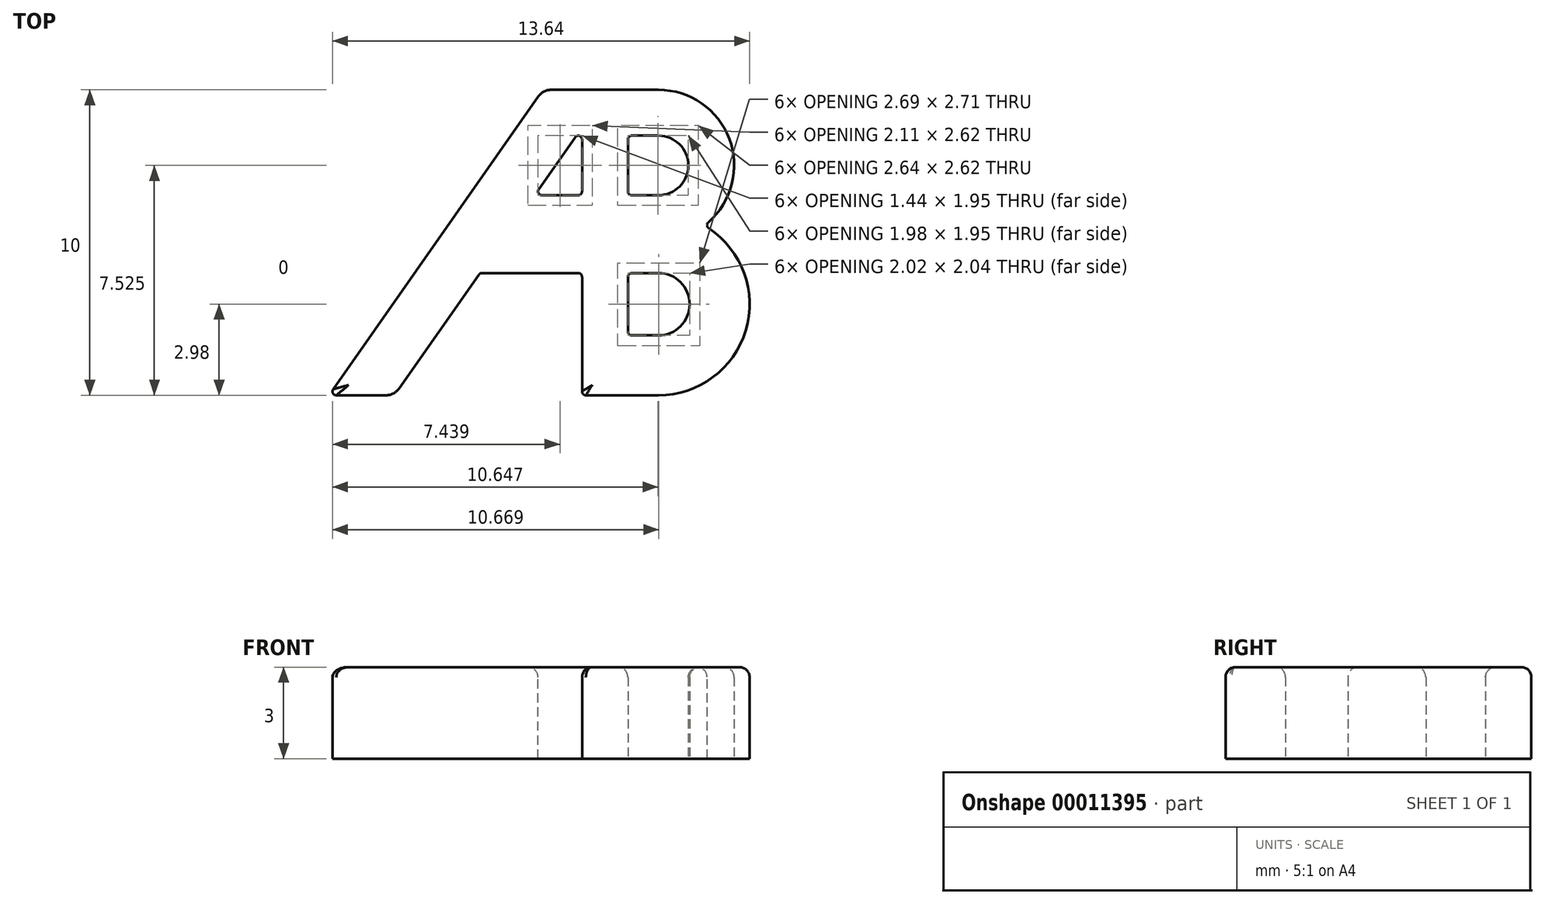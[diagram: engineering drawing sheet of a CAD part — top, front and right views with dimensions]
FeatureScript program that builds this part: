
annotation { "Feature Type Name" : "Feature", "Feature Type Description" : "" }
export const myFeature = defineFeature(function(context is Context, id is Id, definition is map)
    precondition{}
    {
        {
            assignVariable(context, id + "F0", {"name" : "Height", "anyValue" : 10});
        }
        {
            var Q0;
            Q0=qCreatedBy(makeId("Top.planeOp"),FACE);
            var sketch = newSketch(context, id + "F1", { "sketchPlane" : qUnion([Q0])});
            skLineSegment(sketch, "E0", {"start": v(-6.88, -5) * mm, "end": v(0.12, 5) * mm});
            skLineSegment(sketch, "E1", {"start": v(0.12, 5) * mm, "end": v(3.9, 5) * mm});
            skArc(sketch, "E2", {"start": v(3.9, 5) * mm, "mid": v(6.24, 3.32) * mm, "end": v(5.4, 0.56) * mm});
            skLineSegment(sketch, "E3", {"start": v(1.4, -5) * mm, "end": v(3.9, -5) * mm});
            skArc(sketch, "E4", {"start": v(3.9, -5) * mm, "mid": v(6.78, -2.8) * mm, "end": v(5.4, 0.56) * mm});
            skLineSegment(sketch, "E5", {"start": v(1.4, -5) * mm, "end": v(1.4, -1) * mm});
            skLineSegment(sketch, "E6", {"start": v(1.4, -1) * mm, "end": v(-1.94, -1) * mm});
            skLineSegment(sketch, "E7", {"start": v(-1.94, -1) * mm, "end": v(-4.74, -5) * mm});
            skLineSegment(sketch, "E8", {"start": v(-4.74, -5) * mm, "end": v(-6.88, -5) * mm});
            skLineSegment(sketch, "E9", {"start": v(3.9, -5) * mm, "end": v(3.9, 5) * mm, "construction": true});
            skLineSegment(sketch, "E10", {"start": v(3.9, 1.55) * mm, "end": v(2.9, 1.55) * mm});
            skArc(sketch, "E11", {"start": v(3.9, 3.5) * mm, "mid": v(4.87, 2.52) * mm, "end": v(3.9, 1.55) * mm});
            skLineSegment(sketch, "E12", {"start": v(3.9, 3.5) * mm, "end": v(2.9, 3.5) * mm});
            skLineSegment(sketch, "E13", {"start": v(2.9, -3.04) * mm, "end": v(2.9, -1) * mm});
            skLineSegment(sketch, "E14", {"start": v(2.9, -1) * mm, "end": v(3.9, -1) * mm});
            skArc(sketch, "E15", {"start": v(3.9, -1) * mm, "mid": v(4.92, -2.02) * mm, "end": v(3.9, -3.04) * mm});
            skLineSegment(sketch, "E16", {"start": v(2.9, -3.04) * mm, "end": v(3.9, -3.04) * mm});
            skLineSegment(sketch, "E17", {"start": v(2.9, 1.55) * mm, "end": v(2.9, 3.5) * mm});
            skLineSegment(sketch, "E18", {"start": v(1.4, 3.38) * mm, "end": v(1.4, 1.55) * mm});
            skLineSegment(sketch, "E19", {"start": v(1.4, 1.55) * mm, "end": v(-0.16, 1.55) * mm});
            skLineSegment(sketch, "E20", {"start": v(-0.16, 1.55) * mm, "end": v(1.17, 3.45) * mm});
            skLineSegment(sketch, "E21.bottom", {"start": v(-6.88, -5) * mm, "end": v(6.88, -5) * mm, "construction": true});
            skLineSegment(sketch, "E21.top", {"start": v(-6.88, 5) * mm, "end": v(6.88, 5) * mm, "construction": true});
            skLineSegment(sketch, "E21.left", {"start": v(-6.88, -5) * mm, "end": v(-6.88, 5) * mm, "construction": true});
            skLineSegment(sketch, "E21.right", {"start": v(6.88, -5) * mm, "end": v(6.88, 5) * mm, "construction": true});
            skLineSegment(sketch, "E22", {"start": v(-6.88, 5) * mm, "end": v(6.88, -5) * mm, "construction": true});
            skPoint(sketch, "E23.visualSharp", {"position": v(1.4, 3.77) * mm});
            skArc(sketch, "E23.filletArc", {"start": v(1.4, 3.38) * mm, "mid": v(1.31, 3.5) * mm, "end": v(1.17, 3.45) * mm});
            skLineSegment(sketch, "E24", {"start": v(2.9, 3.5) * mm, "end": v(-2.48, 3.5) * mm, "construction": true});
            skSolve(sketch);
        }
        {
            var Q0;
            Q0 = qSketchRegion(id + "F1", true);
            extrude(context, id + "F2", {"entities" : qUnion([Q0]), "depth" : 3 * mm, "offsetDistance" : 25 * mm});
        }
        {
            var Q0;
            Q0=makeQuery(id+"F2.opExtrude","SWEPT_EDGE",EDGE,{"disambiguationData":[OSD([sQuery(id+"F1.wireOp",EDGE,"E18"),sQuery(id+"F1.wireOp",EDGE,"E19")])]});
            var Q1;
            Q1=makeQuery(id+"F2.opExtrude","SWEPT_EDGE",EDGE,{"disambiguationData":[OSD([sQuery(id+"F1.wireOp",EDGE,"E19"),sQuery(id+"F1.wireOp",EDGE,"E20")])]});
            var Q2;
            Q2=makeQuery(id+"F2.opExtrude","SWEPT_EDGE",EDGE,{"disambiguationData":[OSD([sQuery(id+"F1.wireOp",EDGE,"E0"),sQuery(id+"F1.wireOp",EDGE,"E8")])]});
            var Q3;
            Q3=makeQuery(id+"F2.opExtrude","SWEPT_EDGE",EDGE,{"disambiguationData":[OSD([sQuery(id+"F1.wireOp",EDGE,"E6"),sQuery(id+"F1.wireOp",EDGE,"E7")])]});
            var Q4;
            Q4=makeQuery(id+"F2.opExtrude","SWEPT_EDGE",EDGE,{"disambiguationData":[OSD([sQuery(id+"F1.wireOp",EDGE,"E5"),sQuery(id+"F1.wireOp",EDGE,"E6")])]});
            var Q5;
            Q5=makeQuery(id+"F2.opExtrude","SWEPT_EDGE",EDGE,{"disambiguationData":[OSD([sQuery(id+"F1.wireOp",EDGE,"E12"),sQuery(id+"F1.wireOp",EDGE,"E17")])]});
            var Q6;
            Q6=makeQuery(id+"F2.opExtrude","SWEPT_EDGE",EDGE,{"disambiguationData":[OSD([sQuery(id+"F1.wireOp",EDGE,"E13"),sQuery(id+"F1.wireOp",EDGE,"E14")])]});
            var Q7;
            Q7=makeQuery(id+"F2.opExtrude","SWEPT_EDGE",EDGE,{"disambiguationData":[OSD([sQuery(id+"F1.wireOp",EDGE,"E18"),sQuery(id+"F1.wireOp",EDGE,"E19")])]});
            var Q8;
            Q8=makeQuery(id+"F2.opExtrude","SWEPT_EDGE",EDGE,{"disambiguationData":[OSD([sQuery(id+"F1.wireOp",EDGE,"E10"),sQuery(id+"F1.wireOp",EDGE,"E17")])]});
            var Q9;
            Q9=makeQuery(id+"F2.opExtrude","SWEPT_EDGE",EDGE,{"disambiguationData":[OSD([sQuery(id+"F1.wireOp",EDGE,"E13"),sQuery(id+"F1.wireOp",EDGE,"E16")])]});
            var Q10;
            Q10=makeQuery(id+"F2.opExtrude","SWEPT_EDGE",EDGE,{"disambiguationData":[OSD([sQuery(id+"F1.wireOp",EDGE,"E19"),sQuery(id+"F1.wireOp",EDGE,"E20")])]});
            var Q11;
            Q11=makeQuery(id+"F2.opExtrude","SWEPT_EDGE",EDGE,{"disambiguationData":[OSD([sQuery(id+"F1.wireOp",EDGE,"E2"),sQuery(id+"F1.wireOp",EDGE,"E4")])]});
            var Q12;
            Q12=makeQuery(id+"F2.opExtrude","SWEPT_EDGE",EDGE,{"disambiguationData":[OSD([sQuery(id+"F1.wireOp",EDGE,"E3"),sQuery(id+"F1.wireOp",EDGE,"E5")])]});
            fillet(context, id + "F3", {"entities" : qUnion([Q0, Q1, Q2, Q3, Q4, Q5, Q6, Q7, Q8, Q9, Q10, Q11, Q12]), "radius" : (getVariable(context, 'Height') / 80) * mm, "tangentPropagation" : true, "allowEdgeOverflow" : false});
        }
        {
            var Q0;
            Q0=makeQuery(id+"F2.opExtrude","SWEPT_EDGE",EDGE,{"disambiguationData":[OSD([sQuery(id+"F1.wireOp",EDGE,"E0"),sQuery(id+"F1.wireOp",EDGE,"E1")])]});
            var Q1;
            Q1=makeQuery(id+"F2.opExtrude","SWEPT_EDGE",EDGE,{"disambiguationData":[OSD([sQuery(id+"F1.wireOp",EDGE,"E7"),sQuery(id+"F1.wireOp",EDGE,"E8")])]});
            fillet(context, id + "F4", {"entities" : qUnion([Q0, Q1]), "radius" : (getVariable(context, 'Height') / 20) * mm, "tangentPropagation" : true, "allowEdgeOverflow" : false});
        }
        {
            var Q0;
            Q0=makeQuery(id+"F2.opExtrude","CAP_EDGE",EDGE,{"disambiguationData":[OSD([sQuery(id+"F1.wireOp",EDGE,"E0")])],"isStart":false});
            var Q1;
            Q1=makeQuery(id+"F2.opExtrude","CAP_EDGE",EDGE,{"disambiguationData":[OSD([sQuery(id+"F1.wireOp",EDGE,"E17")])],"isStart":false});
            var Q2;
            Q2=makeQuery(id+"F2.opExtrude","CAP_EDGE",EDGE,{"disambiguationData":[OSD([sQuery(id+"F1.wireOp",EDGE,"E18")])],"isStart":false});
            var Q3;
            Q3=makeQuery(id+"F2.opExtrude","CAP_EDGE",EDGE,{"disambiguationData":[OSD([sQuery(id+"F1.wireOp",EDGE,"E13")])],"isStart":false});
            fillet(context, id + "F5", {"entities" : qUnion([Q0, Q1, Q2, Q3]), "radius" : (getVariable(context, 'Height') / 30) * mm, "tangentPropagation" : true, "allowEdgeOverflow" : false});
        }
    });
